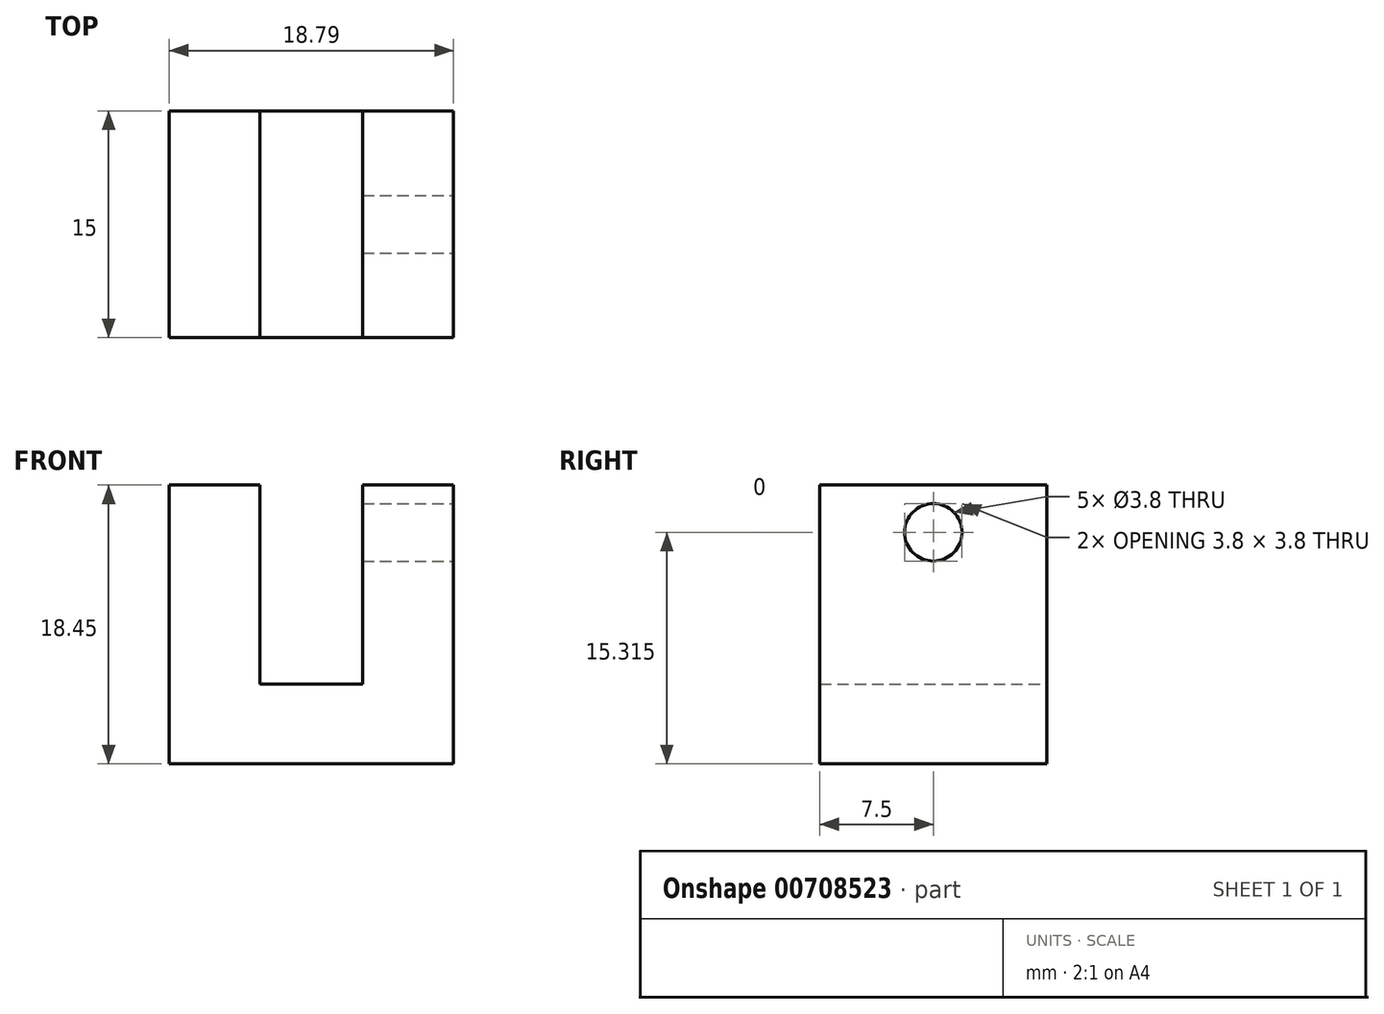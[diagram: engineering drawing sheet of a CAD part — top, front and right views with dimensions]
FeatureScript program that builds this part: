
annotation { "Feature Type Name" : "Feature", "Feature Type Description" : "" }
export const myFeature = defineFeature(function(context is Context, id is Id, definition is map)
    precondition{}
    {
        {
            var Q0;
            Q0=qCreatedBy(makeId("Front.planeOp"),FACE);
            var sketch = newSketch(context, id + "F0", { "sketchPlane" : qUnion([Q0])});
            skLineSegment(sketch, "E0", {"start": v(0, 0) * mm, "end": v(0, 18.45) * mm});
            skLineSegment(sketch, "E1.bottom", {"start": v(14.93, -9.66) * mm, "end": v(19.91, -9.66) * mm});
            skLineSegment(sketch, "E1.top", {"start": v(14.93, -24.3) * mm, "end": v(19.91, -24.3) * mm});
            skLineSegment(sketch, "E1.left", {"start": v(14.93, -9.66) * mm, "end": v(14.93, -24.3) * mm});
            skLineSegment(sketch, "E1.right", {"start": v(19.91, -9.66) * mm, "end": v(19.91, -24.3) * mm});
            skLineSegment(sketch, "E2.bottom", {"start": v(14.93, -24.3) * mm, "end": v(26.94, -24.3) * mm});
            skLineSegment(sketch, "E2.top", {"start": v(14.93, -30.45) * mm, "end": v(26.94, -30.45) * mm});
            skLineSegment(sketch, "E2.left", {"start": v(14.93, -24.3) * mm, "end": v(14.93, -30.45) * mm});
            skLineSegment(sketch, "E2.right", {"start": v(26.94, -24.3) * mm, "end": v(26.94, -30.45) * mm});
            skLineSegment(sketch, "E3.bottom", {"start": v(26.94, -24.3) * mm, "end": v(32.8, -24.3) * mm});
            skLineSegment(sketch, "E3.top", {"start": v(26.94, -30.45) * mm, "end": v(32.8, -30.45) * mm});
            skLineSegment(sketch, "E3.right", {"start": v(32.8, -24.3) * mm, "end": v(32.8, -30.45) * mm});
            skLineSegment(sketch, "E4.bottom", {"start": v(31.92, -9.66) * mm, "end": v(26.94, -9.66) * mm});
            skLineSegment(sketch, "E4.top", {"start": v(31.92, -9.66) * mm, "end": v(26.94, -9.66) * mm});
            skLineSegment(sketch, "E4.left", {"start": v(31.92, -9.66) * mm, "end": v(31.92, -9.66) * mm});
            skLineSegment(sketch, "E4.right", {"start": v(26.94, -9.66) * mm, "end": v(26.94, -9.66) * mm});
            skLineSegment(sketch, "E5", {"start": v(0, 18.45) * mm, "end": v(6, 18.45) * mm});
            skLineSegment(sketch, "E6", {"start": v(6, 18.45) * mm, "end": v(6, 5.3) * mm});
            skLineSegment(sketch, "E7", {"start": v(6, 5.3) * mm, "end": v(12.8, 5.3) * mm});
            skLineSegment(sketch, "E8", {"start": v(12.8, 5.3) * mm, "end": v(12.8, 18.45) * mm});
            skLineSegment(sketch, "E9", {"start": v(12.8, 18.45) * mm, "end": v(18.8, 18.45) * mm});
            skLineSegment(sketch, "E10", {"start": v(18.8, 18.45) * mm, "end": v(18.8, 0) * mm});
            skLineSegment(sketch, "E11", {"start": v(18.8, 0) * mm, "end": v(0, 0) * mm});
            skSolve(sketch);
        }
        {
            var Q0;
            Q0=makeQuery(id+"F0.imprint","IMPRINT",FACE,{"disambiguationData":[TD([[makeQuery(id+"F0.imprint","IMPRINT",EDGE,{"derivedFrom":sQuery(id+"F0.wireOp",EDGE,"E0")}),-1.0]])]});
            extrude(context, id + "F1", {"entities" : qUnion([Q0]), "depth" : 15 * mm, "offsetDistance" : 25 * mm});
        }
        {
            var Q0;
            Q0=makeQuery(id+"F1.opExtrude","SWEPT_FACE",FACE,{"disambiguationData":[OSD([sQuery(id+"F0.wireOp",EDGE,"E10")])]});
            var sketch = newSketch(context, id + "F2", { "sketchPlane" : qUnion([Q0])});
            skPoint(sketch, "E12", {"position": v(-7.5, 15.32) * mm});
            skPoint(sketch, "E12.positionSnap0", {"position": v(-7.5, 18.45) * mm});
            skSolve(sketch);
        }
        {
            var Q0;
            Q0=sQuery(id+"F2.wireOp",VERTEX,"E12");
            var Q1;
            Q1=makeQuery(id+"F1.opExtrude","SWEPT_BODY",BODY,{"disambiguationData":[OSD([sQuery(id+"F0.wireOp",EDGE,"E0"),sQuery(id+"F0.wireOp",EDGE,"E5"),sQuery(id+"F0.wireOp",EDGE,"E6"),sQuery(id+"F0.wireOp",EDGE,"E7"),sQuery(id+"F0.wireOp",EDGE,"E8"),sQuery(id+"F0.wireOp",EDGE,"E9"),sQuery(id+"F0.wireOp",EDGE,"E10"),sQuery(id+"F0.wireOp",EDGE,"E11")])]});
            hole(context, id + "F3", {"style" : HoleStyle.SIMPLE, "endStyle" : HoleEndStyle.BLIND, "holeDiameter" : 3.8 * mm, "majorDiameter" : 5 * mm, "holeDepth" : 8 * mm, "isTappedThrough" : true, "tappedDepth" : 12 * mm, "tapClearance" : 3, "startFromSketch" : true, "locations" : qUnion([Q0]), "scope" : qUnion([Q1])});
        }
    });
